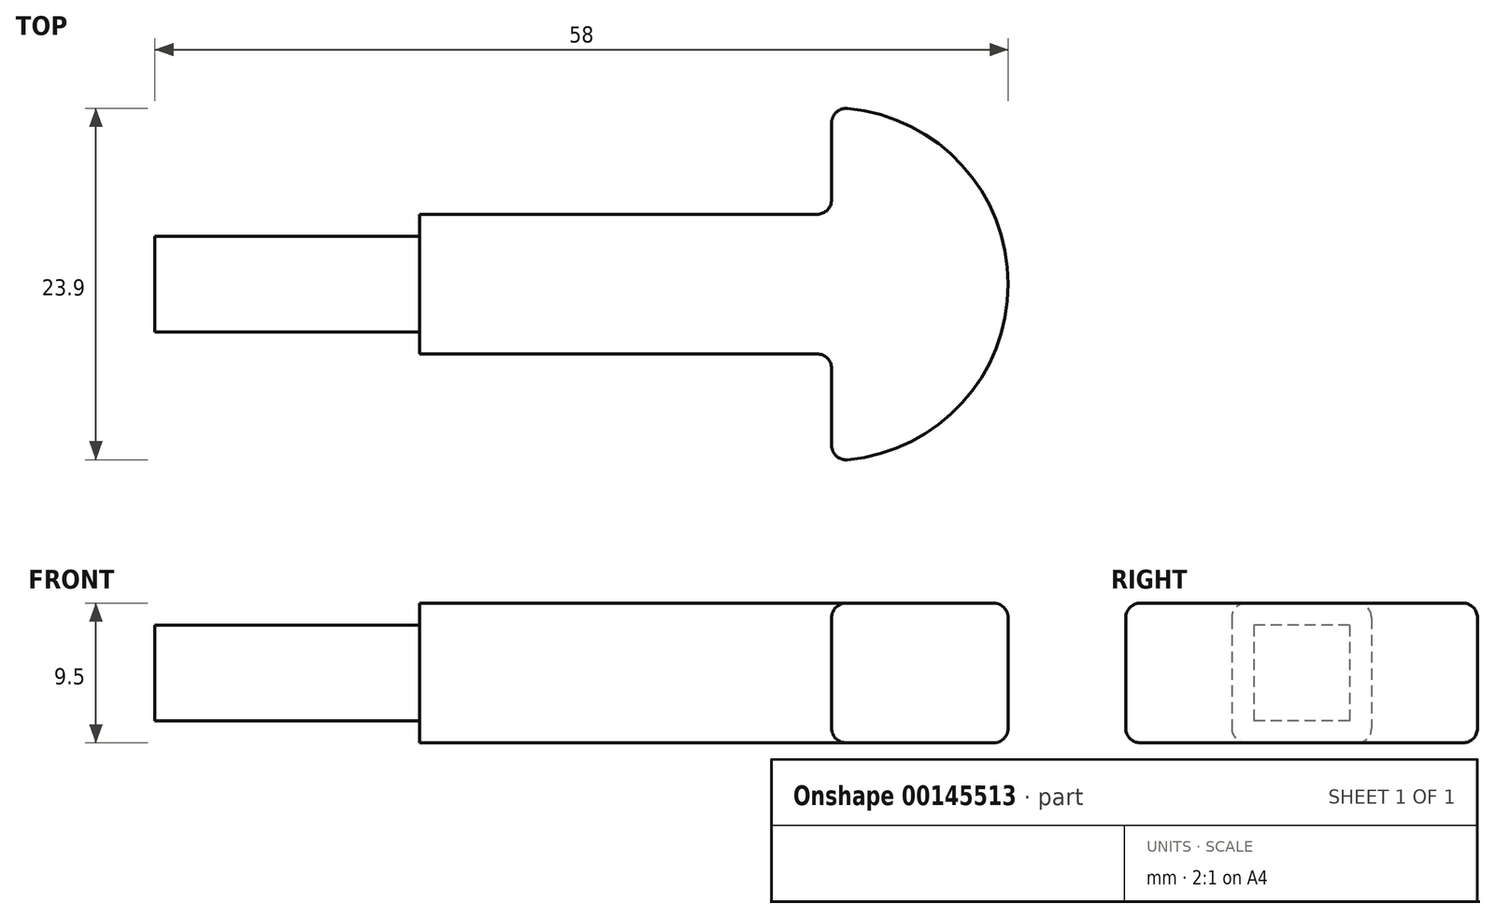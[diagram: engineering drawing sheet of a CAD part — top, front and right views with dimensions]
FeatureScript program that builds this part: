
annotation { "Feature Type Name" : "Feature", "Feature Type Description" : "" }
export const myFeature = defineFeature(function(context is Context, id is Id, definition is map)
    precondition{}
    {
        {
            var Q0;
            Q0=qCreatedBy(makeId("Top.planeOp"),FACE);
            var sketch = newSketch(context, id + "F0", { "sketchPlane" : qUnion([Q0])});
            skLineSegment(sketch, "E0.bottom", {"start": v(-5, 3.25) * mm, "end": v(-23, 3.25) * mm});
            skLineSegment(sketch, "E0.top", {"start": v(-5, -3.25) * mm, "end": v(-23, -3.25) * mm});
            skLineSegment(sketch, "E0.right", {"start": v(-23, 3.25) * mm, "end": v(-23, -3.25) * mm});
            skPoint(sketch, "E0.middle", {"position": v(0, 0) * mm});
            skLineSegment(sketch, "E1", {"start": v(23, 4.75) * mm, "end": v(23, 12) * mm});
            skLineSegment(sketch, "E2", {"start": v(23, -4.75) * mm, "end": v(23, -12) * mm});
            skArc(sketch, "E3", {"start": v(23, 12) * mm, "mid": v(35, 0) * mm, "end": v(23, -12) * mm});
            skPoint(sketch, "E4.orphan", {"position": v(23, 3.25) * mm});
            skPoint(sketch, "E5.orphan", {"position": v(23, -3.25) * mm});
            skLineSegment(sketch, "E6", {"start": v(-23, -3.25) * mm, "end": v(-7.12, -3.25) * mm, "construction": true});
            skLineSegment(sketch, "E7", {"start": v(-7.12, 3.25) * mm, "end": v(-23, 3.25) * mm, "construction": true});
            skLineSegment(sketch, "E8", {"start": v(-5, -3.25) * mm, "end": v(-5, -4.75) * mm});
            skLineSegment(sketch, "E9", {"start": v(-5, -4.75) * mm, "end": v(23, -4.75) * mm});
            skLineSegment(sketch, "E10", {"start": v(-5, 3.25) * mm, "end": v(-5, 4.75) * mm});
            skLineSegment(sketch, "E11", {"start": v(-5, 4.75) * mm, "end": v(23, 4.75) * mm});
            skSolve(sketch);
        }
        {
            var Q0;
            Q0 = qSketchRegion(id + "F0", true);
            extrude(context, id + "F1", {"entities" : qUnion([Q0]), "depth" : 9.5 * mm});
        }
        {
            var Q0;
            Q0=makeQuery(id+"F1.opExtrude","CAP_EDGE",EDGE,{"disambiguationData":[OSD([sQuery(id+"F0.wireOp",EDGE,"E1")])],"isStart":false});
            var Q1;
            Q1=makeQuery(id+"F1.opExtrude","CAP_EDGE",EDGE,{"disambiguationData":[OSD([sQuery(id+"F0.wireOp",EDGE,"E1")])],"isStart":true});
            var Q2;
            Q2=makeQuery(id+"F1.opExtrude","CAP_EDGE",EDGE,{"disambiguationData":[OSD([sQuery(id+"F0.wireOp",EDGE,"E2")])],"isStart":false});
            var Q3;
            Q3=makeQuery(id+"F1.opExtrude","CAP_EDGE",EDGE,{"disambiguationData":[OSD([sQuery(id+"F0.wireOp",EDGE,"E2")])],"isStart":true});
            var Q4;
            Q4=makeQuery(id+"F1.opExtrude","SWEPT_EDGE",EDGE,{"disambiguationData":[OSD([sQuery(id+"F0.wireOp",EDGE,"E2"),sQuery(id+"F0.wireOp",EDGE,"E3")])]});
            var Q5;
            Q5=makeQuery(id+"F1.opExtrude","SWEPT_EDGE",EDGE,{"disambiguationData":[OSD([sQuery(id+"F0.wireOp",EDGE,"E1"),sQuery(id+"F0.wireOp",EDGE,"E3")])]});
            var Q6;
            Q6=makeQuery(id+"F1.opExtrude","CAP_EDGE",EDGE,{"disambiguationData":[OSD([sQuery(id+"F0.wireOp",EDGE,"E3")])],"isStart":false});
            var Q7;
            Q7=makeQuery(id+"F1.opExtrude","CAP_EDGE",EDGE,{"disambiguationData":[OSD([sQuery(id+"F0.wireOp",EDGE,"E3")])],"isStart":true});
            fillet(context, id + "F2", {"entities" : qUnion([Q0, Q1, Q2, Q3, Q4, Q5, Q6, Q7]), "radius" : 1 * mm, "tangentPropagation" : true, "allowEdgeOverflow" : false});
        }
        {
            var Q0;
            Q0=makeQuery(id+"F1.opExtrude","CAP_EDGE",EDGE,{"disambiguationData":[OSD([sQuery(id+"F0.wireOp",EDGE,"E11")])],"isStart":true});
            var Q1;
            Q1=makeQuery(id+"F1.opExtrude","CAP_EDGE",EDGE,{"disambiguationData":[OSD([sQuery(id+"F0.wireOp",EDGE,"E11")])],"isStart":false});
            var Q2;
            Q2=makeQuery(id+"F1.opExtrude","SWEPT_EDGE",EDGE,{"disambiguationData":[OSD([sQuery(id+"F0.wireOp",EDGE,"E1"),sQuery(id+"F0.wireOp",EDGE,"E11")])]});
            var Q3;
            Q3=makeQuery(id+"F1.opExtrude","SWEPT_EDGE",EDGE,{"disambiguationData":[OSD([sQuery(id+"F0.wireOp",EDGE,"E2"),sQuery(id+"F0.wireOp",EDGE,"E9")])]});
            var Q4;
            Q4=makeQuery(id+"F1.opExtrude","CAP_EDGE",EDGE,{"disambiguationData":[OSD([sQuery(id+"F0.wireOp",EDGE,"E9")])],"isStart":false});
            var Q5;
            Q5=makeQuery(id+"F1.opExtrude","CAP_EDGE",EDGE,{"disambiguationData":[OSD([sQuery(id+"F0.wireOp",EDGE,"E9")])],"isStart":true});
            fillet(context, id + "F3", {"entities" : qUnion([Q0, Q1, Q2, Q3, Q4, Q5]), "radius" : 1 * mm, "tangentPropagation" : true, "allowEdgeOverflow" : false});
        }
        {
            var Q0;
            Q0=makeQuery(id+"F1.opExtrude","SWEPT_FACE",FACE,{"disambiguationData":[OSD([sQuery(id+"F0.wireOp",EDGE,"E0.right")])]});
            var sketch = newSketch(context, id + "F4", { "sketchPlane" : qUnion([Q0])});
            skLineSegment(sketch, "E12.bottom", {"start": v(-3.25, 9.5) * mm, "end": v(3.25, 9.5) * mm});
            skLineSegment(sketch, "E12.top", {"start": v(-3.25, 8) * mm, "end": v(3.25, 8) * mm});
            skLineSegment(sketch, "E12.left", {"start": v(-3.25, 9.5) * mm, "end": v(-3.25, 8) * mm});
            skLineSegment(sketch, "E12.right", {"start": v(3.25, 9.5) * mm, "end": v(3.25, 8) * mm});
            skLineSegment(sketch, "E13.bottom", {"start": v(-3.25, 0) * mm, "end": v(3.25, 0) * mm});
            skLineSegment(sketch, "E13.top", {"start": v(-3.25, 1.5) * mm, "end": v(3.25, 1.5) * mm});
            skLineSegment(sketch, "E13.left", {"start": v(-3.25, 0) * mm, "end": v(-3.25, 1.5) * mm});
            skLineSegment(sketch, "E13.right", {"start": v(3.25, 0) * mm, "end": v(3.25, 1.5) * mm});
            skSolve(sketch);
        }
        {
            var Q0;
            Q0 = qSketchRegion(id + "F4", true);
            extrude(context, id + "F5", {"entities" : qUnion([Q0]), "operationType" : NewBodyOperationType.REMOVE, "oppositeDirection" : true, "depth" : 18 * mm});
        }
    });
